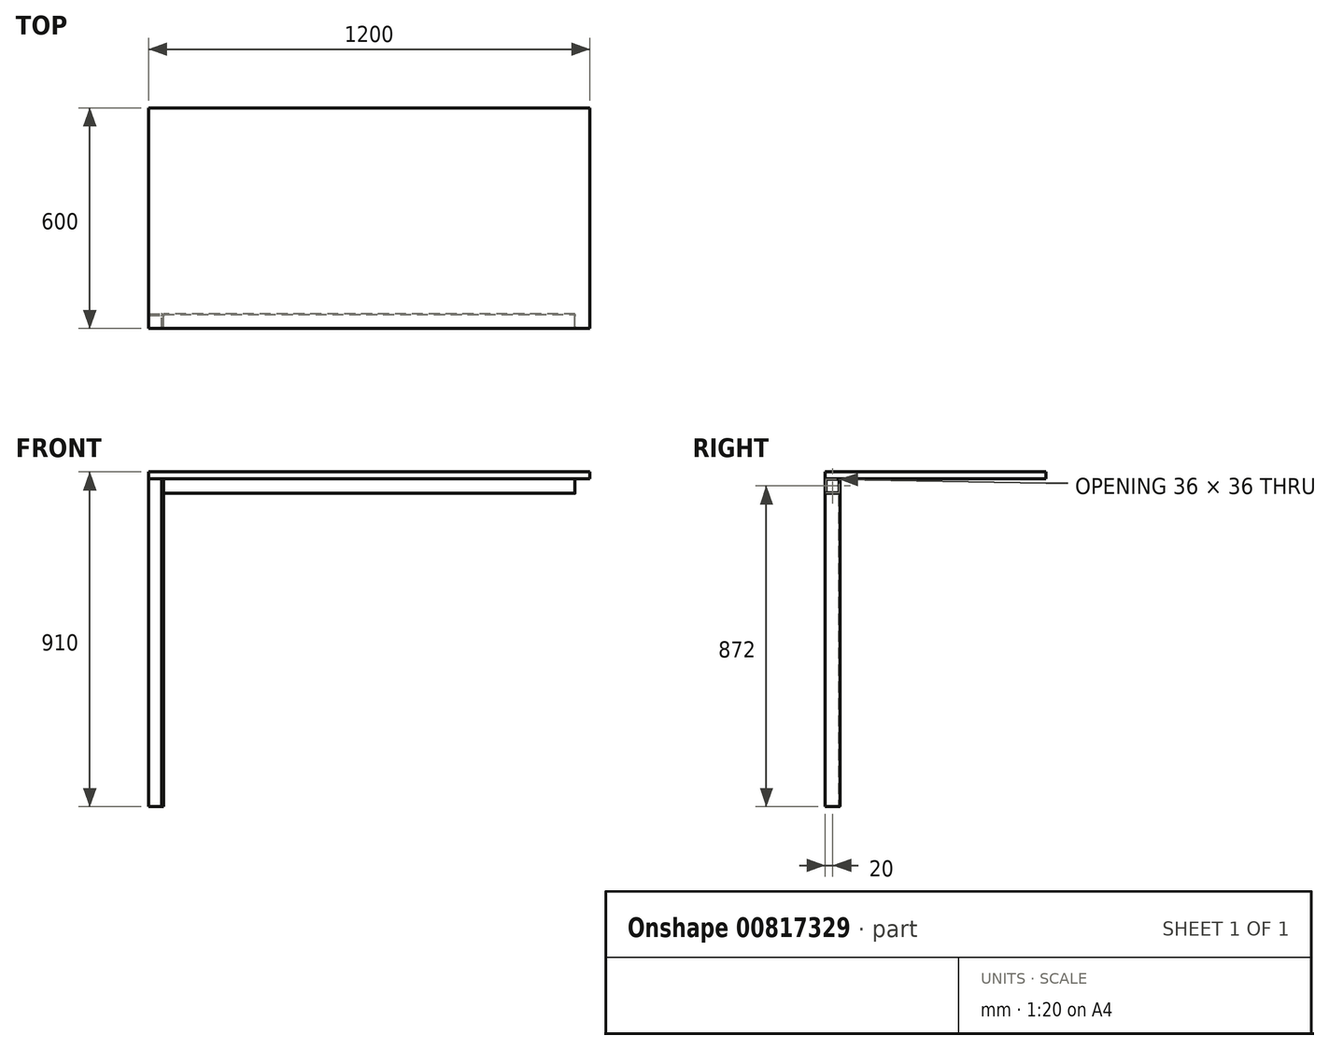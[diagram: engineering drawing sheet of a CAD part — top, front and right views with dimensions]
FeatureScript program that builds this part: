
annotation { "Feature Type Name" : "Feature", "Feature Type Description" : "" }
export const myFeature = defineFeature(function(context is Context, id is Id, definition is map)
    precondition{}
    {
        {
            var Q0;
            Q0=qCreatedBy(makeId("Top.planeOp"),FACE);
            cPlane(context, id + "F0", {"entities" : qUnion([Q0]), "cplaneType" : CPlaneType.OFFSET, "offset" : 1010 * mm, "width" : 152.4 * mm, "height" : 152.4 * mm});
        }
        {
            var Q0;
            Q0=qCreatedBy(makeId("Top.planeOp"),FACE);
            cPlane(context, id + "F1", {"entities" : qUnion([Q0]), "cplaneType" : CPlaneType.OFFSET, "offset" : 100 * mm, "width" : 150 * mm, "height" : 150 * mm});
        }
        {
            var Q0;
            Q0=qCreatedBy(id+"F0.planeOp",FACE);
            var sketch = newSketch(context, id + "F2", { "sketchPlane" : qUnion([Q0])});
            skLineSegment(sketch, "E0.bottom", {"start": v(0, 0) * mm, "end": v(1200, 0) * mm});
            skLineSegment(sketch, "E0.top", {"start": v(0, 600) * mm, "end": v(1200, 600) * mm});
            skLineSegment(sketch, "E0.left", {"start": v(0, 0) * mm, "end": v(0, 600) * mm});
            skLineSegment(sketch, "E0.right", {"start": v(1200, 0) * mm, "end": v(1200, 600) * mm});
            skSolve(sketch);
        }
        {
            var Q0;
            Q0 = qSketchRegion(id + "F2", true);
            extrude(context, id + "F3", {"entities" : qUnion([Q0]), "oppositeDirection" : true, "depth" : 18 * mm, "offsetDistance" : 25 * mm});
        }
        {
            var Q0;
            Q0=qCreatedBy(id+"F1.planeOp",FACE);
            var sketch = newSketch(context, id + "F4", { "sketchPlane" : qUnion([Q0])});
            skLineSegment(sketch, "E1.bottom", {"start": v(0, 0) * mm, "end": v(40, 0) * mm, "construction": true});
            skLineSegment(sketch, "E1.top", {"start": v(0, 40) * mm, "end": v(34, 40) * mm});
            skLineSegment(sketch, "E1.left", {"start": v(0, 0) * mm, "end": v(0, 40) * mm, "construction": true});
            skLineSegment(sketch, "E1.right", {"start": v(40, 0) * mm, "end": v(40, 34) * mm});
            skLineSegment(sketch, "E2.0", {"start": v(36, 0) * mm, "end": v(36, 34) * mm});
            skLineSegment(sketch, "E2.1", {"start": v(0, 36) * mm, "end": v(34, 36) * mm});
            skLineSegment(sketch, "E3", {"start": v(0, 36) * mm, "end": v(0, 40) * mm});
            skLineSegment(sketch, "E4", {"start": v(36, 0) * mm, "end": v(40, 0) * mm});
            skPoint(sketch, "E5.visualSharp", {"position": v(40, 40) * mm});
            skArc(sketch, "E5.filletArc", {"start": v(40, 34) * mm, "mid": v(38.24, 38.24) * mm, "end": v(34, 40) * mm});
            skPoint(sketch, "E6.visualSharp", {"position": v(36, 36) * mm});
            skArc(sketch, "E6.filletArc", {"start": v(36, 34) * mm, "mid": v(35.41, 35.41) * mm, "end": v(34, 36) * mm});
            skSolve(sketch);
        }
        {
            var Q0;
            Q0 = qSketchRegion(id + "F4", true);
            var Q1;
            Q1=makeQuery(id+"F3.opExtrude","CAP_FACE",FACE,{"disambiguationData":[OSD([sQuery(id+"F2.wireOp",EDGE,"E0.bottom"),sQuery(id+"F2.wireOp",EDGE,"E0.top"),sQuery(id+"F2.wireOp",EDGE,"E0.left"),sQuery(id+"F2.wireOp",EDGE,"E0.right")])],"isStart":false});
            var Q2;
            Q2=makeQuery(id+"F3.opExtrude","SWEPT_BODY",BODY,{"disambiguationData":[OSD([sQuery(id+"F2.wireOp",EDGE,"E0.bottom"),sQuery(id+"F2.wireOp",EDGE,"E0.top"),sQuery(id+"F2.wireOp",EDGE,"E0.left"),sQuery(id+"F2.wireOp",EDGE,"E0.right")])]});
            extrude(context, id + "F5", {"entities" : qUnion([Q0]), "endBound" : BoundingType.UP_TO_SURFACE, "depth" : 25 * mm, "endBoundEntityFace" : qUnion([Q1]), "endBoundEntityBody" : qUnion([Q2]), "offsetDistance" : 25 * mm});
        }
        {
            var Q0;
            Q0=makeQuery(id+"F5.opExtrude","SWEPT_FACE",FACE,{"disambiguationData":[OSD([sQuery(id+"F4.wireOp",EDGE,"E1.right")])]});
            var sketch = newSketch(context, id + "F6", { "sketchPlane" : qUnion([Q0])});
            skLineSegment(sketch, "E7.bottom", {"start": v(0, 992) * mm, "end": v(40, 992) * mm});
            skLineSegment(sketch, "E7.top", {"start": v(0, 952) * mm, "end": v(40, 952) * mm});
            skLineSegment(sketch, "E7.left", {"start": v(0, 992) * mm, "end": v(0, 952) * mm});
            skLineSegment(sketch, "E7.right", {"start": v(40, 992) * mm, "end": v(40, 952) * mm});
            skSolve(sketch);
        }
        {
            var Q0;
            Q0 = qSketchRegion(id + "F6", true);
            var Q1;
            Q1=makeQuery(id+"F3.opExtrude","SWEPT_FACE",FACE,{"disambiguationData":[OSD([sQuery(id+"F2.wireOp",EDGE,"E0.right")])]});
            extrude(context, id + "F7", {"entities" : qUnion([Q0]), "depth" : (1200 - 80) * mm, "endBoundEntityFace" : qUnion([Q1]), "offsetDistance" : 25 * mm});
        }
        {
            var Q0;
            Q0=makeQuery(id+"F7.opExtrude","SWEPT_EDGE",EDGE,{"disambiguationData":[OSD([sQuery(id+"F6.wireOp",EDGE,"E7.bottom"),sQuery(id+"F6.wireOp",EDGE,"E7.right")])]});
            var Q1;
            Q1=makeQuery(id+"F7.opExtrude","SWEPT_EDGE",EDGE,{"disambiguationData":[OSD([sQuery(id+"F6.wireOp",EDGE,"E7.top"),sQuery(id+"F6.wireOp",EDGE,"E7.right")])]});
            var Q2;
            Q2=makeQuery(id+"F7.opExtrude","SWEPT_EDGE",EDGE,{"disambiguationData":[OSD([sQuery(id+"F6.wireOp",EDGE,"E7.bottom"),sQuery(id+"F6.wireOp",EDGE,"E7.left")])]});
            var Q3;
            Q3=makeQuery(id+"F7.opExtrude","SWEPT_EDGE",EDGE,{"disambiguationData":[OSD([sQuery(id+"F4.wireOp",EDGE,"E1.right"),sQuery(id+"F4.wireOp",EDGE,"E4"),sQuery(id+"F6.wireOp",EDGE,"E7.top"),sQuery(id+"F6.wireOp",EDGE,"E7.left")])]});
            fillet(context, id + "F8", {"entities" : qUnion([Q0, Q1, Q2, Q3]), "radius" : 6 * mm, "tangentPropagation" : true, "allowEdgeOverflow" : false});
        }
        {
            var Q0;
            Q0=makeQuery(id+"F7.opExtrude","CAP_FACE",FACE,{"disambiguationData":[OSD([sQuery(id+"F6.wireOp",EDGE,"E7.bottom"),sQuery(id+"F6.wireOp",EDGE,"E7.top"),sQuery(id+"F6.wireOp",EDGE,"E7.left"),sQuery(id+"F6.wireOp",EDGE,"E7.right")])],"isStart":false});
            var Q1;
            Q1=makeQuery(id+"F7.opExtrude","CAP_FACE",FACE,{"disambiguationData":[OSD([sQuery(id+"F6.wireOp",EDGE,"E7.bottom"),sQuery(id+"F6.wireOp",EDGE,"E7.top"),sQuery(id+"F6.wireOp",EDGE,"E7.left"),sQuery(id+"F6.wireOp",EDGE,"E7.right")])],"isStart":true});
            var Q2;
            Q2=makeQuery(id+"F7.opExtrude","SWEPT_BODY",BODY,{"disambiguationData":[OSD([sQuery(id+"F6.wireOp",EDGE,"E7.bottom"),sQuery(id+"F6.wireOp",EDGE,"E7.top"),sQuery(id+"F6.wireOp",EDGE,"E7.left"),sQuery(id+"F6.wireOp",EDGE,"E7.right")])]});
            shell(context, id + "F9", {"entities" : qUnion([Q0, Q1]), "parts" : qUnion([Q2]), "thickness" : 2 * mm});
        }
    });
